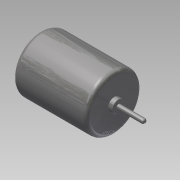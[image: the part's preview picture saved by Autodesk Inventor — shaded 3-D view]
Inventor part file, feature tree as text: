
AUTODESK INVENTOR PART (.ipt)
format: ipt  version: 2015 SP1 (Build 190203100, 203)  size: 615,936 bytes
history: native  units: mm
features: extrude x7, sketch x5, fillet x5
ambient origin geometry x8: Origin, YZ Plane, XZ Plane, XY Plane, X Axis, Y Axis, Z Axis, Center Point
bodies: Solid1 (feature_tree)
feature tree (17):
  sketch  "Sketch1"  dims[d0=25.37mm d1=5.66mm]
  extrude  "Extrusion1"  Depth=5.66mm
  extrude  "Extrusion2"  Depth=33.86mm TaperAngle=0.0deg
  extrude  "Extrusion3"  Depth=14.28mm TaperAngle=0.0deg
  fillet  "Fillet1"  Radius=2.0mm
  fillet  "Fillet2"  Radius=0.25mm
  fillet  "Fillet3"  Radius=1.0mm
  sketch  "Sketch2"  dims[d2=2.1mm d3=33.86mm d4=0.0mm]
  extrude  "Extrusion4"  Depth=2.0mm TaperAngle=0.0deg
  extrude  "Extrusion5"  Depth=0.25mm
  fillet  "Fillet4"  Radius=1.0mm
  fillet  "Fillet5"  Radius=10.0mm
  extrude  "Extrusion6"  Depth=10.0mm TaperAngle=0.0deg
  extrude  "Extrusion7"  [1 undecoded]
  sketch  "Sketch6"  dims[d15=2.62mm d16=0.0mm d17=0.25mm d18=1.0mm d19=10.0mm d20=0.0mm d21=10.0mm d22=0.0mm]
  sketch  "Sketch4"  dims[d5=2.0mm d6=0.0mm d7=14.28mm d8=0.0mm d9=2.0mm d10=0.25mm d11=1.0mm]
  sketch  "Sketch5"  dims[d12=2.0mm d13=2.0mm d14=0.0mm]
note: 1 required parameter value undecoded (feature->parameter linkage not recoverable at this tier; creation-order binding heuristic only, values carry confidence <= 0.55)
